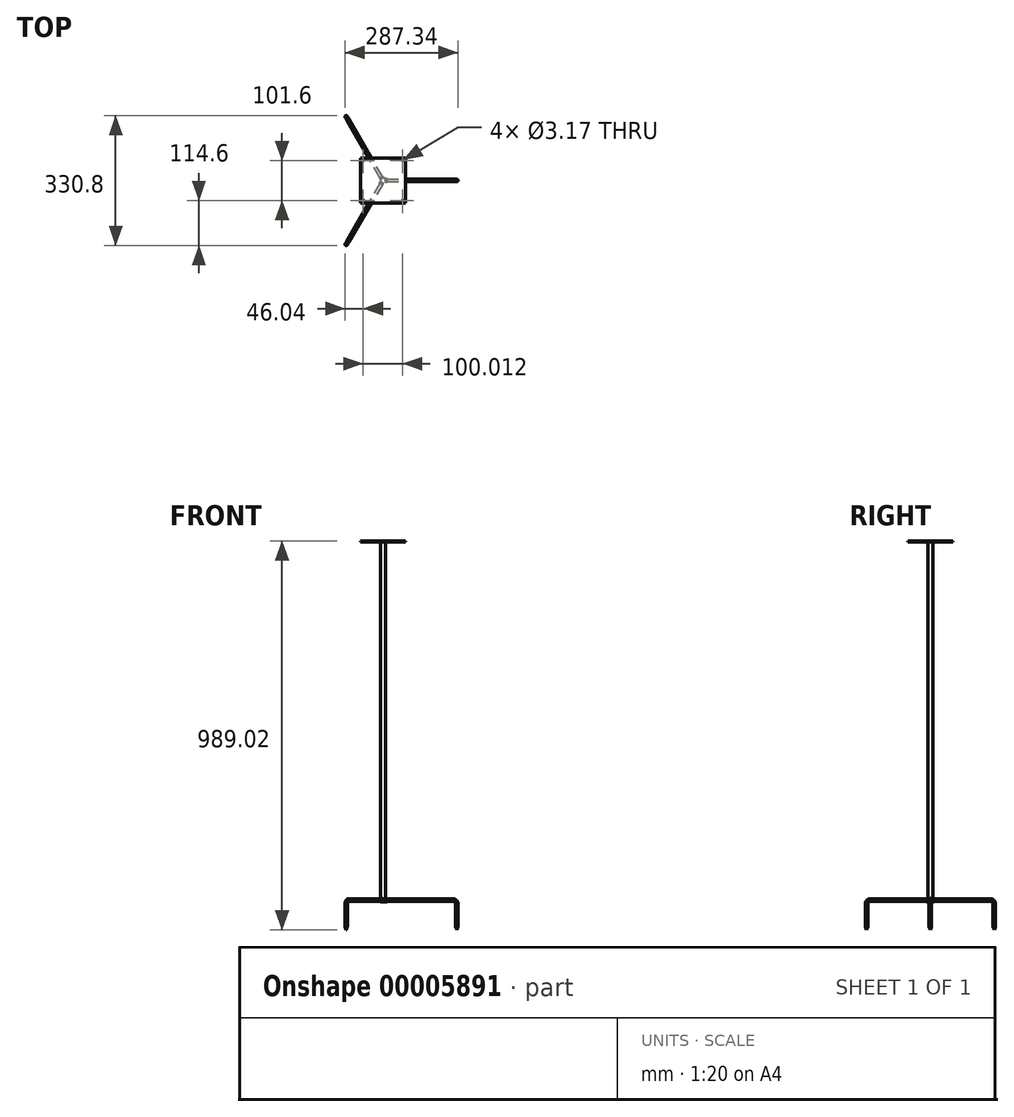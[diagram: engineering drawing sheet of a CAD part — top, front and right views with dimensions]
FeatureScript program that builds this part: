
annotation { "Feature Type Name" : "Feature", "Feature Type Description" : "" }
export const myFeature = defineFeature(function(context is Context, id is Id, definition is map)
    precondition{}
    {
        {
            var Q0;
            Q0=qCreatedBy(makeId("Top.planeOp"),FACE);
            var sketch = newSketch(context, id + "F0", { "sketchPlane" : qUnion([Q0])});
            skCircle(sketch, "E0", {"center": v(0, 0) * mm, "radius": 6.35 * mm});
            skSolve(sketch);
        }
        {
            var Q0;
            Q0 = qSketchRegion(id + "F0", true);
            extrude(context, id + "F1", {"entities" : qUnion([Q0]), "depth" : 914.4 * mm});
        }
        {
            var Q0;
            Q0=qCreatedBy(makeId("Right.planeOp"),FACE);
            cPlane(context, id + "F2", {"entities" : qUnion([Q0]), "cplaneType" : CPlaneType.OFFSET, "offset" : 6.35 * mm, "width" : 152.4 * mm, "height" : 152.4 * mm});
        }
        {
            var Q0;
            Q0=qCreatedBy(id+"F2.planeOp",FACE);
            var sketch = newSketch(context, id + "F3", { "sketchPlane" : qUnion([Q0])});
            skCircle(sketch, "E1", {"center": v(0, 4.76) * mm, "radius": 4.76 * mm});
            skSolve(sketch);
        }
        {
            var Q0;
            Q0=makeQuery(id+"F3.imprint","IMPRINT",FACE,{"disambiguationData":[TD([[makeQuery(id+"F3.imprint","IMPRINT",EDGE,{"derivedFrom":sQuery(id+"F3.wireOp",EDGE,"E1")}),1.0]])]});
            extrude(context, id + "F4", {"entities" : qUnion([Q0]), "operationType" : NewBodyOperationType.ADD, "depth" : 3.17 * mm});
        }
        {
            var Q0;
            Q0=makeQuery(id+"F4.opExtrude","CAP_FACE",FACE,{"disambiguationData":[OSD([sQuery(id+"F3.wireOp",EDGE,"E1")])],"isStart":false});
            var sketch = newSketch(context, id + "F5", { "sketchPlane" : qUnion([Q0])});
            skCircle(sketch, "E2", {"center": v(0, 4.76) * mm, "radius": 3.18 * mm});
            skSolve(sketch);
        }
        {
            var Q0;
            Q0=qCreatedBy(makeId("Front.planeOp"),FACE);
            var sketch = newSketch(context, id + "F6", { "sketchPlane" : qUnion([Q0])});
            skLineSegment(sketch, "E3", {"start": v(9.52, 4.76) * mm, "end": v(177.8, 4.76) * mm});
            skPoint(sketch, "E4.0", {"position": v(9.53, 4.76) * mm});
            skLineSegment(sketch, "E5", {"start": v(187.33, -4.76) * mm, "end": v(187.33, -71.44) * mm});
            skPoint(sketch, "E6.visualSharp", {"position": v(187.32, 4.76) * mm});
            skArc(sketch, "E6.filletArc", {"start": v(187.33, -4.76) * mm, "mid": v(184.54, 1.97) * mm, "end": v(177.8, 4.76) * mm});
            skSolve(sketch);
        }
        {
            var Q0;
            Q0=makeQuery(id+"F5.imprint","IMPRINT",FACE,{"disambiguationData":[TD([[makeQuery(id+"F5.imprint","IMPRINT",EDGE,{"derivedFrom":sQuery(id+"F5.wireOp",EDGE,"E2")}),1.0]])]});
            var Q1;
            Q1=sQuery(id+"F6.wireOp",EDGE,"E3");
            var Q2;
            Q2=sQuery(id+"F6.wireOp",EDGE,"E6.filletArc");
            var Q3;
            Q3=sQuery(id+"F6.wireOp",EDGE,"E5");
            sweep(context, id + "F7", {"profiles" : qUnion([Q0]), "path" : qUnion([Q1, Q2, Q3])});
        }
        {
            var Q0;
            Q0=makeQuery(id+"F7.opSweep","SWEPT_BODY",BODY,{"disambiguationData":[OSD([sQuery(id+"F5.wireOp",EDGE,"E2"),sQuery(id+"F6.wireOp",EDGE,"E5")])]});
            var Q1;
            Q1=makeQuery(id+"F4.opExtrude","SWEPT_BODY",BODY,{"disambiguationData":[OSD([sQuery(id+"F3.wireOp",EDGE,"E1")])]});
            var Q2;
            Q2=makeQuery(id+"F1.opExtrude","SWEPT_FACE",FACE,{"disambiguationData":[OSD([sQuery(id+"F0.wireOp",EDGE,"E0")])]});
            circularPattern(context, id + "F8", {"entities" : qUnion([Q0, Q1]), "axis" : qUnion([Q2]), "angle" : 360 * degree, "instanceCount" : 3, "equalSpace" : true});
        }
        {
            var Q0;
            Q0=makeQuery(id+"F1.opExtrude","CAP_FACE",FACE,{"disambiguationData":[OSD([sQuery(id+"F0.wireOp",EDGE,"E0")])],"isStart":false});
            var sketch = newSketch(context, id + "F9", { "sketchPlane" : qUnion([Q0])});
            skLineSegment(sketch, "E7.rect.bottom", {"start": v(-57.15, -57.15) * mm, "end": v(57.15, -57.15) * mm});
            skLineSegment(sketch, "E7.rect.top", {"start": v(-57.15, 57.15) * mm, "end": v(57.15, 57.15) * mm});
            skLineSegment(sketch, "E7.rect.left", {"start": v(-57.15, -57.15) * mm, "end": v(-57.15, 57.15) * mm});
            skLineSegment(sketch, "E7.rect.right", {"start": v(57.15, -57.15) * mm, "end": v(57.15, 57.15) * mm});
            skPoint(sketch, "E7.rect.middle", {"position": v(0, 0) * mm});
            skCircle(sketch, "E8", {"center": v(49.21, 50.8) * mm, "radius": 1.59 * mm});
            skCircle(sketch, "E9", {"center": v(-50.8, 50.8) * mm, "radius": 1.59 * mm});
            skCircle(sketch, "E10", {"center": v(-50.8, -50.8) * mm, "radius": 1.59 * mm});
            skCircle(sketch, "E11", {"center": v(49.21, -50.8) * mm, "radius": 1.59 * mm});
            skSolve(sketch);
        }
        {
            var Q0;
            Q0 = qSketchRegion(id + "F9", true);
            extrude(context, id + "F10", {"entities" : qUnion([Q0]), "operationType" : NewBodyOperationType.ADD, "depth" : 3.17 * mm});
        }
        {
            var Q0;
            Q0=makeQuery(id+"F8.opPattern","COPY",EDGE,{"derivedFrom":makeQuery(id+"F7.opSweep","CAP_EDGE",EDGE,{"disambiguationData":[OSD([sQuery(id+"F5.wireOp",EDGE,"E2"),sQuery(id+"F6.wireOp",VERTEX,"E5.end")])],"isStart":false}),"instanceName":"1"});
            var Q1;
            Q1=makeQuery(id+"F7.opSweep","CAP_EDGE",EDGE,{"disambiguationData":[OSD([sQuery(id+"F5.wireOp",EDGE,"E2"),sQuery(id+"F6.wireOp",VERTEX,"E5.end")])],"isStart":false});
            var Q2;
            Q2=makeQuery(id+"F8.opPattern","COPY",EDGE,{"derivedFrom":makeQuery(id+"F7.opSweep","CAP_EDGE",EDGE,{"disambiguationData":[OSD([sQuery(id+"F5.wireOp",EDGE,"E2"),sQuery(id+"F6.wireOp",VERTEX,"E5.end")])],"isStart":false}),"instanceName":"2"});
            chamfer(context, id + "F11", {"entities" : qUnion([Q0, Q1, Q2]), "chamferType" : ChamferType.OFFSET_ANGLE, "width" : 3.17 * mm, "oppositeDirection" : false, "angle" : 70 * degree, "tangentPropagation" : true});
        }
    });
